# Revit family: CU2SO
name_source: partatom
category: Lighting Fixtures
units: mm (PartAtom-declared; Revit-internal decimal feet)

## family parameters
Cut with Voids When Loaded = No
Host = Face
Light Source = No
OmniClass Number = 23.80.70.11
OmniClass Title = Luminaries for Internal Lighting
Part Type = Normal
Room Calculation Point = No
Round Connector Dimension = Use Diameter
Shared = No

## types (1)
- CU2SO
    Apparent Load = 4 VA
    Application = Rain and Severe moisture. Some of these include outside over
doors, in parking garages, around pools or in basements.
    Backbox = Paint- White
    Certification = UL924 Listed for Damp Location
NFPA 101 and NFPA 70
OSHA
    Default Elevation = 48 "
    Description = LED emergency light with fully adjustable lampheads, gasketed polycarbonate shield for outdoor use, Nickel Cadmium battery
    Features = LED Life-cycle of more than 10 years
•	 Quick Installation
•	 Dual-Voltage 102/277VAC Input
•	 Includes long-life Nickel Cadmium battery for UL
recognized 90 minute emergency lighting
•	 Wet Location Listed 0°C to 40°C (32°F to 104°F)
•	 Fully Adjustable lamp-heads
•	 Includes test switch and AC-On indicator
    Glass = White Glass
    LED = White Glass
    Lamp = LED Lamp
    Manufacturer = Compass Products
    Model = CU2SO
    Nominal Watts = 4 W
    Steel = Metal-Galvanized_Steel
    URL = https://www.currentlighting.com
    Voltage = 120 V
    Warranty = 2Year full unit warranty
    Wattage Comments = 3.6W

## geometry (parser evidence)
native form markers: Sweep x5
no freeform markers — native parametric forms only
